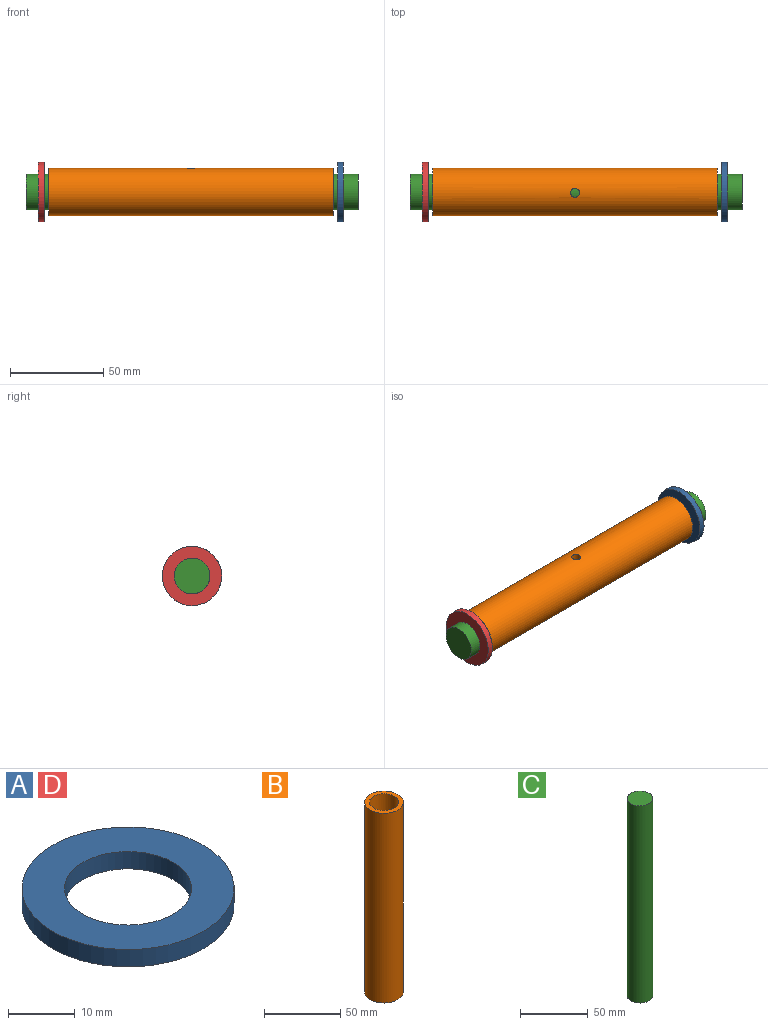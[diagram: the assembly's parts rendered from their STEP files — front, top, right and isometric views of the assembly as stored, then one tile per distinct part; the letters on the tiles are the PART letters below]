
ASSEMBLY  parts=4 mates=3
PART A: 4 faces, bbox 31.8x31.8x3.2 mm
  f0: cylinder r=9.53mm len=19.05mm, axis (0,0,-1), area 190mm2, adj f2,f3
  f1: cylinder r=15.88mm len=31.75mm, axis (0,0,-1), area 316.7mm2, adj f2,f3
  f2: plane 31.75x31.75mm, normal (0,0,1), area 506.7mm2, adj f0,f1
  f3: plane 31.75x31.75mm, normal (0,0,-1), area 506.7mm2, adj f0,f1
PART B: 5 faces, bbox 25.4x25.4x152.4 mm
  f0: cylinder r=9.53mm len=152.4mm, axis (0,0,-1), area 9102.8mm2, adj f2,f3,f4
  f1: cylinder r=12.7mm len=152.4mm, axis (0,0,-1), area 12143.1mm2, adj f2,f3,f4
  f2: plane 25.4x25.4mm, normal (0,0,1), area 221.7mm2, adj f0,f1
  f3: plane 25.4x25.4mm, normal (0,0,-1), area 221.7mm2, adj f0,f1
  f4: cylinder r=2.38mm len=4.76mm, axis (-1,0,0), area 48.1mm2, adj f0,f1
PART C: 3 faces, bbox 19.1x19.1x177.8 mm
  f0: cylinder r=9.53mm len=177.8mm, axis (0,0,-1), area 10640.9mm2, adj f1,f2
  f1: plane 19.05x19.05mm, normal (0,0,1), area 285mm2, adj f0
  f2: plane 19.05x19.05mm, normal (0,0,-1), area 285mm2, adj f0
PART D: same geometry as A
PLACE A rot(axis=(-0.53,-0.66,0.53),113deg) t=(109.12,0,0)mm
PLACE B rot(axis=(0.02,-1,-0.02),90deg) t=(103.72,0,0)mm
PLACE C rot(axis=(0.08,-0.99,-0.08),90.4deg) t=(116.91,0,0)mm
PLACE D rot(axis=(-0.54,0.64,-0.54),114.6deg) t=(-54.36,0,0)mm
MATE cylindrical A.f0 <-> C.f0  axis (1,0,0) through (109.12,0,0)mm
MATE cylindrical D.f0 <-> C.f0  axis (-1,0,0) through (-54.36,0,0)mm
MATE cylindrical B.f0 <-> C.f0  axis (1,0,0) through (-48.68,0,0)mm
